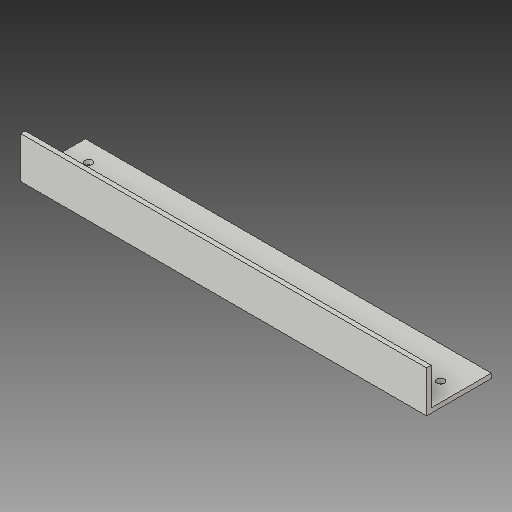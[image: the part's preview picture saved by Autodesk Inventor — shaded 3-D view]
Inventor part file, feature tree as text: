
AUTODESK INVENTOR PART (.ipt)
format: ipt  version: 2018 (Build 220112000, 112)  size: 126,976 bytes
history: native  units: in
note: dims shown in document units (in); Inventor stores cm internally (conversion verified against a paired STEP export)
features: extrude x4, sketch x4
ambient origin geometry x8: Origin, YZ Plane, XZ Plane, XY Plane, X Axis, Y Axis, Z Axis, Center Point
bodies: Solid1 (feature_tree)
feature tree (8):
  extrude  "Extrusion1"  Depth=1.755in
  extrude  "Extrusion2"  Depth=11.0in
  extrude  "Extrusion3"  Depth=1.0in TaperAngle=0.0deg
  extrude  "Extrusion4"  Depth=1.0in
  sketch  "Sketch1"  dims[d0=11.0in d1=1.755in]
  sketch  "Sketch2"  dims[d2=0.125in d3=0.0in d4=11.0in]
  sketch  "Sketch3"  dims[d5=0.125in d6=1.0in d7=0.0in]
  sketch  "Sketch4"  dims[d14=1.0in d15=0.0in d26=0.5in d27=0.875in d28=0.2031in d29=1.0in d30=0.0in]
